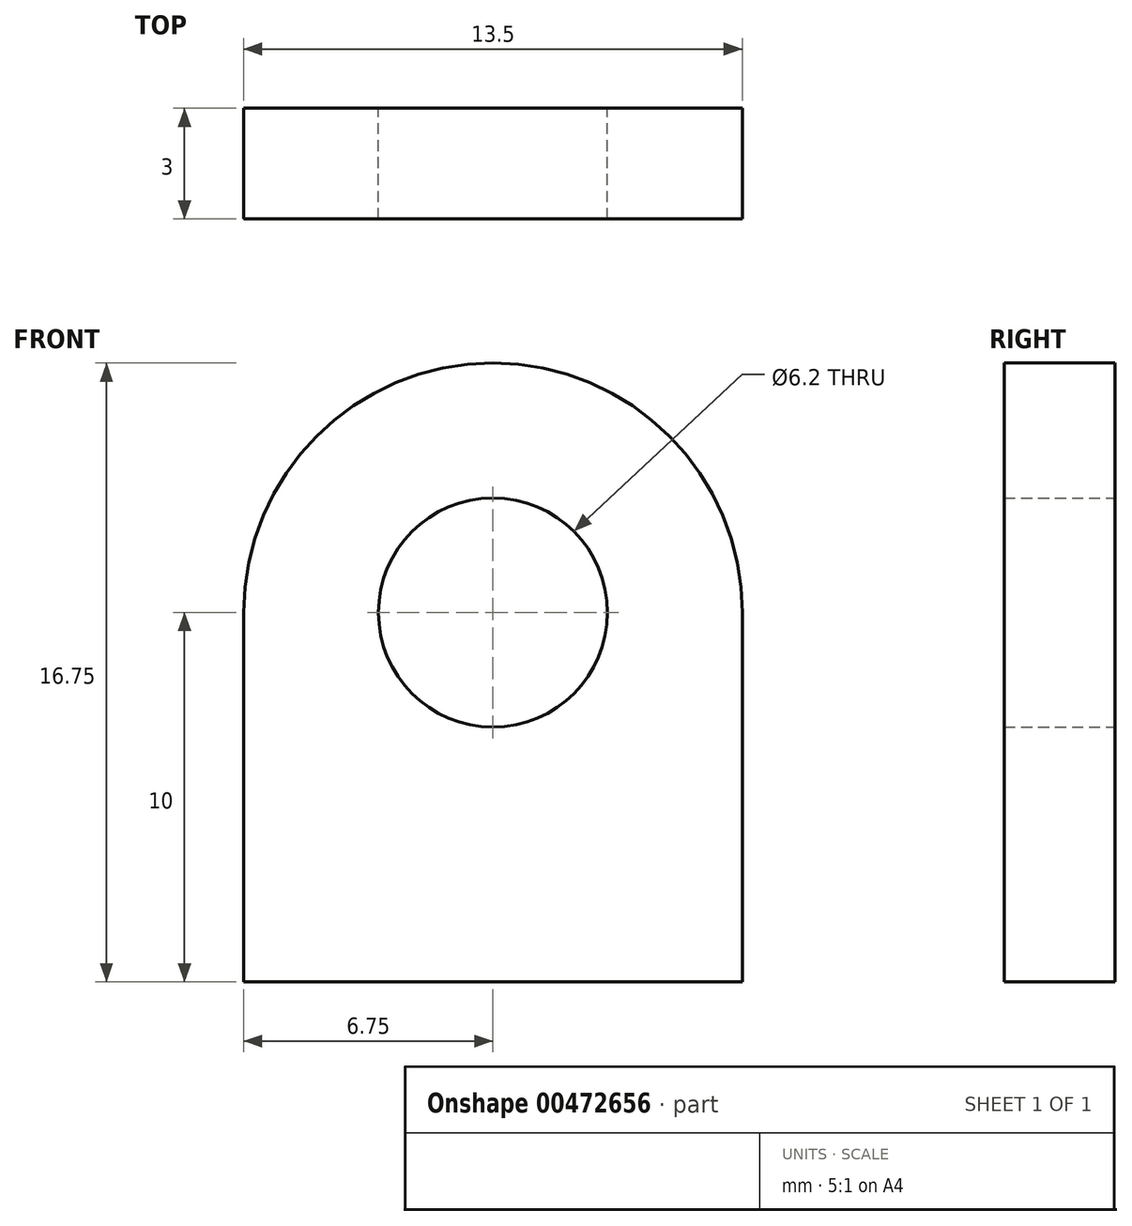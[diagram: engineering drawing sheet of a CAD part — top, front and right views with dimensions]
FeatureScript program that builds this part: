
annotation { "Feature Type Name" : "Feature", "Feature Type Description" : "" }
export const myFeature = defineFeature(function(context is Context, id is Id, definition is map)
    precondition{}
    {
        {
            var Q0;
            Q0=qCreatedBy(makeId("Front.planeOp"),FACE);
            var sketch = newSketch(context, id + "F0", { "sketchPlane" : qUnion([Q0])});
            skArc(sketch, "E0", {"start": v(6.75, 0) * mm, "mid": v(0, 6.75) * mm, "end": v(-6.75, 0) * mm});
            skLineSegment(sketch, "E1", {"start": v(-6.75, 0) * mm, "end": v(-6.75, -10) * mm});
            skLineSegment(sketch, "E2", {"start": v(6.75, 0) * mm, "end": v(6.75, -10) * mm});
            skCircle(sketch, "E3", {"center": v(0, 0) * mm, "radius": 3.1 * mm});
            skLineSegment(sketch, "E4", {"start": v(-6.75, -10) * mm, "end": v(6.75, -10) * mm});
            skSolve(sketch);
        }
        {
            var Q0;
            Q0 = qSketchRegion(id + "F0", true);
            extrude(context, id + "F1", {"entities" : qUnion([Q0]), "depth" : 3 * mm});
        }
    });
